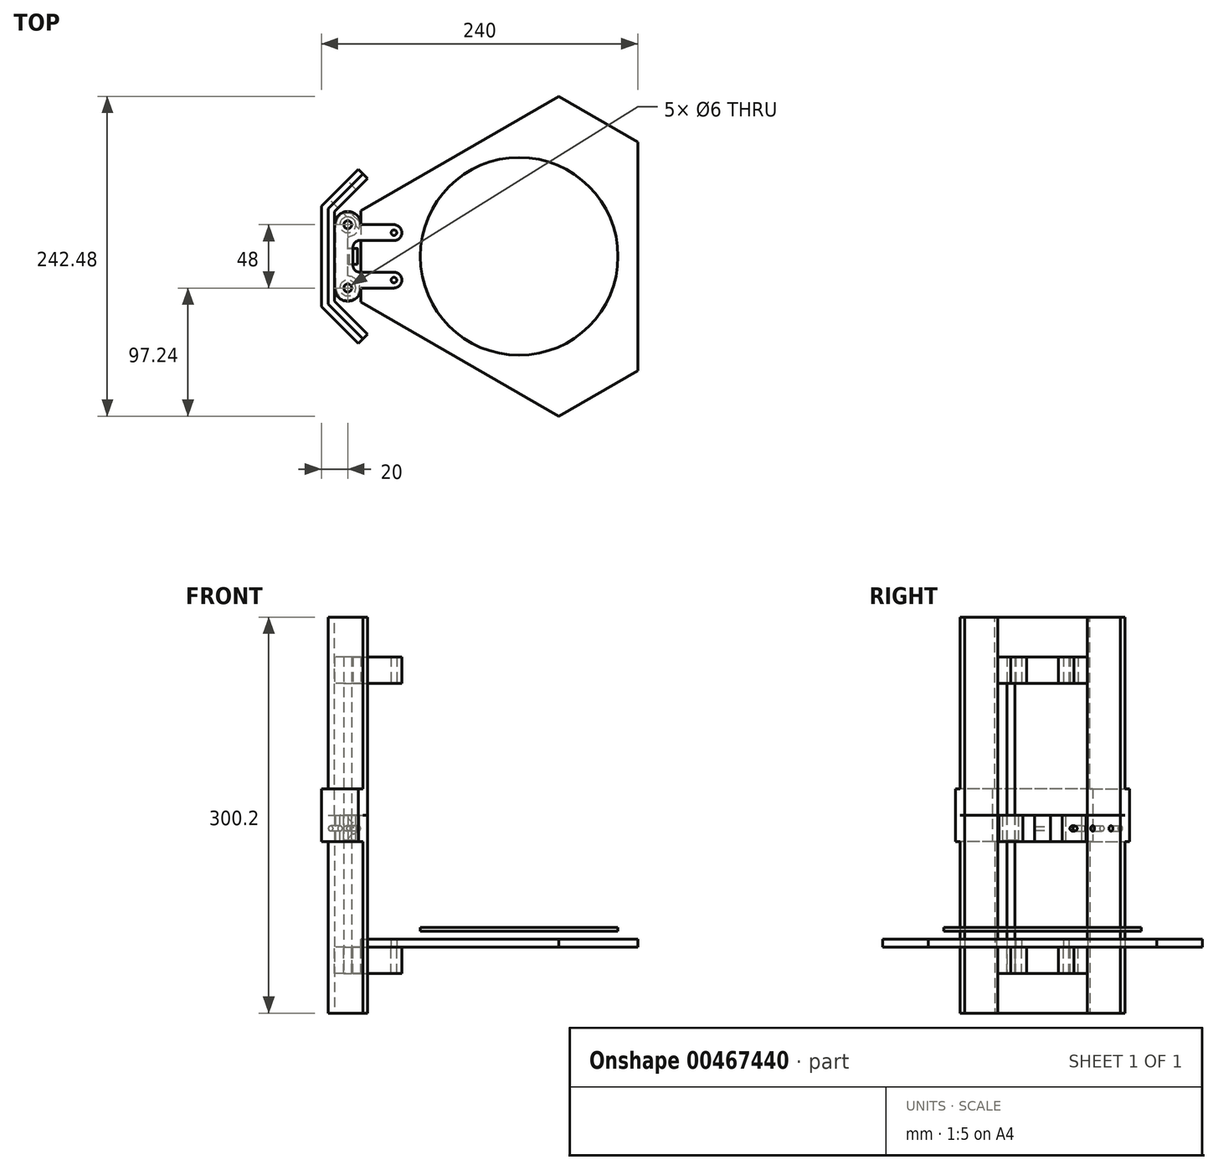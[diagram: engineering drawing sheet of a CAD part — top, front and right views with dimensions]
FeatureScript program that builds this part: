
annotation { "Feature Type Name" : "Feature", "Feature Type Description" : "" }
export const myFeature = defineFeature(function(context is Context, id is Id, definition is map)
    precondition{}
    {
        {
            var Q0;
            Q0=qCreatedBy(makeId("Top.planeOp"),FACE);
            var sketch = newSketch(context, id + "F0", { "sketchPlane" : qUnion([Q0])});
            skCircle(sketch, "E0", {"center": v(0, 0) * mm, "radius": 75 * mm});
            skSolve(sketch);
        }
        {
            var Q0;
            Q0=makeQuery(id+"F0.imprint","IMPRINT",FACE,{"disambiguationData":[TD([[makeQuery(id+"F0.imprint","IMPRINT",EDGE,{"derivedFrom":sQuery(id+"F0.wireOp",EDGE,"E0")}),1.0]])]});
            extrude(context, id + "F1", {"entities" : qUnion([Q0]), "depth" : 3 * mm});
        }
        {
            var Q0;
            Q0=qCreatedBy(makeId("Top.planeOp"),FACE);
            cPlane(context, id + "F2", {"entities" : qUnion([Q0]), "cplaneType" : CPlaneType.OFFSET, "offset" : 6 * mm, "oppositeDirection" : true, "width" : 150 * mm, "height" : 150 * mm});
        }
        {
            var Q0;
            Q0=qCreatedBy(id+"F2.planeOp",FACE);
            var sketch = newSketch(context, id + "F3", { "sketchPlane" : qUnion([Q0])});
            skLineSegment(sketch, "E1", {"start": v(30, 121.24) * mm, "end": v(-120, 34.64) * mm});
            skLineSegment(sketch, "E2", {"start": v(-120, 34.64) * mm, "end": v(-120, -34.64) * mm});
            skLineSegment(sketch, "E3", {"start": v(-120, 0) * mm, "end": v(0, 0) * mm, "construction": true});
            skLineSegment(sketch, "E4.1.0", {"start": v(30, -121.24) * mm, "end": v(90, -86.6) * mm});
            skLineSegment(sketch, "E4.1.1", {"start": v(-120, -34.64) * mm, "end": v(30, -121.24) * mm});
            skLineSegment(sketch, "E4.2.0", {"start": v(90, 86.6) * mm, "end": v(30, 121.24) * mm});
            skLineSegment(sketch, "E4.2.1", {"start": v(90, -86.6) * mm, "end": v(90, 86.6) * mm});
            skPoint(sketch, "E4.center", {"position": v(0, 0) * mm});
            skCircle(sketch, "E5", {"center": v(0, 0) * mm, "radius": 90 * mm, "construction": true});
            skSolve(sketch);
        }
        {
            var Q0;
            Q0=makeQuery(id+"F3.imprint","IMPRINT",FACE,{"disambiguationData":[TD([[makeQuery(id+"F3.imprint","IMPRINT",EDGE,{"derivedFrom":sQuery(id+"F3.wireOp",EDGE,"E1")}),1.0]])]});
            extrude(context, id + "F4", {"entities" : qUnion([Q0]), "oppositeDirection" : true, "depth" : 6 * mm});
        }
        {
            var Q0;
            Q0=makeQuery(id+"F4.opExtrude","CAP_FACE",FACE,{"disambiguationData":[OSD([sQuery(id+"F3.wireOp",EDGE,"E1"),sQuery(id+"F3.wireOp",EDGE,"E2"),sQuery(id+"F3.wireOp",EDGE,"E4.1.0"),sQuery(id+"F3.wireOp",EDGE,"E4.1.1"),sQuery(id+"F3.wireOp",EDGE,"E4.2.0"),sQuery(id+"F3.wireOp",EDGE,"E4.2.1")])],"isStart":false});
            var sketch = newSketch(context, id + "F5", { "sketchPlane" : qUnion([Q0])});
            skLineSegment(sketch, "E6", {"start": v(-120, 0) * mm, "end": v(-90, 0) * mm, "construction": true});
            skPoint(sketch, "E6.endSnap0", {"position": v(-120, 0) * mm});
            skLineSegment(sketch, "E7", {"start": v(-120, 18) * mm, "end": v(-95, 18) * mm, "construction": true});
            skArc(sketch, "E8.0.endCap", {"start": v(-95, 24) * mm, "mid": v(-89, 18) * mm, "end": v(-95, 12) * mm});
            skLineSegment(sketch, "E8.0.left", {"start": v(-120, 24) * mm, "end": v(-95, 24) * mm});
            skLineSegment(sketch, "E8.0.right", {"start": v(-119.48, 12) * mm, "end": v(-95, 12) * mm});
            skArc(sketch, "E9.MirrorCS", {"start": v(-95, -24) * mm, "mid": v(-89, -18) * mm, "end": v(-95, -12) * mm});
            skLineSegment(sketch, "E10.MirrorCS", {"start": v(-120, -24) * mm, "end": v(-95, -24) * mm});
            skLineSegment(sketch, "E11.MirrorCS", {"start": v(-119.48, -12) * mm, "end": v(-95, -12) * mm});
            skCircle(sketch, "E12", {"center": v(-95, 18) * mm, "radius": 2.1 * mm});
            skCircle(sketch, "E13", {"center": v(-95, -18) * mm, "radius": 2.1 * mm});
            skLineSegment(sketch, "E14", {"start": v(-140, 24) * mm, "end": v(-140, -24) * mm});
            skLineSegment(sketch, "E15", {"start": v(-126, 7) * mm, "end": v(-126, -7) * mm});
            skPoint(sketch, "E16.orphan", {"position": v(-120, -24) * mm});
            skPoint(sketch, "E17.MirrorCS.start.orphan", {"position": v(-119.48, -12) * mm});
            skLineSegment(sketch, "E18", {"start": v(-119.48, -12) * mm, "end": v(-121, -12) * mm});
            skLineSegment(sketch, "E19", {"start": v(-119.48, 12) * mm, "end": v(-121, 12) * mm});
            skArc(sketch, "E20", {"start": v(-121, 12) * mm, "mid": v(-124.54, 10.54) * mm, "end": v(-126, 7) * mm});
            skArc(sketch, "E21.MirrorCS", {"start": v(-121, -12) * mm, "mid": v(-124.54, -10.54) * mm, "end": v(-126, -7) * mm});
            skCircle(sketch, "E22", {"center": v(-130, -24) * mm, "radius": 3 * mm});
            skArc(sketch, "E23", {"start": v(-140, -24) * mm, "mid": v(-130, -34) * mm, "end": v(-120, -24) * mm});
            skCircle(sketch, "E24.MirrorC", {"center": v(-130, 24) * mm, "radius": 3 * mm});
            skArc(sketch, "E25.MirrorCS", {"start": v(-140, 24) * mm, "mid": v(-130, 34) * mm, "end": v(-120, 24) * mm});
            skSolve(sketch);
        }
        {
            var Q0;
            Q0=qSketchRegion(id+"F5",true);
            extrude(context, id + "F6", {"entities" : qUnion([Q0]), "depth" : 20 * mm});
        }
        {
            var Q0;
            Q0=makeQuery(id+"F4.opExtrude","CAP_FACE",FACE,{"disambiguationData":[OSD([sQuery(id+"F3.wireOp",EDGE,"E1"),sQuery(id+"F3.wireOp",EDGE,"E2"),sQuery(id+"F3.wireOp",EDGE,"E4.1.0"),sQuery(id+"F3.wireOp",EDGE,"E4.1.1"),sQuery(id+"F3.wireOp",EDGE,"E4.2.0"),sQuery(id+"F3.wireOp",EDGE,"E4.2.1")])],"isStart":false});
            cPlane(context, id + "F7", {"entities" : qUnion([Q0]), "cplaneType" : CPlaneType.OFFSET, "offset" : 50 * mm, "width" : 150 * mm, "height" : 150 * mm});
        }
        {
            var Q0;
            Q0=qCreatedBy(id+"F7.planeOp",FACE);
            var sketch = newSketch(context, id + "F8", { "sketchPlane" : qUnion([Q0])});
            skLineSegment(sketch, "E26", {"start": v(-140, -34) * mm, "end": v(-140, 34) * mm});
            skLineSegment(sketch, "E27", {"start": v(-140, 34) * mm, "end": v(-115, 59) * mm});
            skLineSegment(sketch, "E28", {"start": v(-140, 0) * mm, "end": v(-105.12, 0) * mm, "construction": true});
            skLineSegment(sketch, "E29.MirrorCS", {"start": v(-140, -34) * mm, "end": v(-115, -59) * mm});
            skLineSegment(sketch, "E30.0", {"start": v(-145, 36.07) * mm, "end": v(-118.54, 62.54) * mm});
            skLineSegment(sketch, "E30.1", {"start": v(-145, -36.07) * mm, "end": v(-145, 36.07) * mm});
            skLineSegment(sketch, "E30.2", {"start": v(-145, -36.07) * mm, "end": v(-118.54, -62.54) * mm});
            skLineSegment(sketch, "E31", {"start": v(-115, 59) * mm, "end": v(-118.54, 62.54) * mm});
            skLineSegment(sketch, "E32", {"start": v(-115, -59) * mm, "end": v(-118.54, -62.54) * mm});
            skSolve(sketch);
        }
        {
            var Q0;
            Q0=makeQuery(id+"F8.imprint","IMPRINT",FACE,{"disambiguationData":[TD([[makeQuery(id+"F8.imprint","IMPRINT",EDGE,{"derivedFrom":sQuery(id+"F8.wireOp",EDGE,"E26")}),1.0]])]});
            extrude(context, id + "F9", {"entities" : qUnion([Q0]), "operationType" : NewBodyOperationType.ADD, "oppositeDirection" : true, "depth" : 150 * mm});
        }
        {
            var Q0;
            Q0=makeQuery(id+"F9.opExtrude","CAP_FACE",FACE,{"disambiguationData":[OSD([sQuery(id+"F8.wireOp",EDGE,"E26"),sQuery(id+"F8.wireOp",EDGE,"E27"),sQuery(id+"F8.wireOp",EDGE,"E29.MirrorCS"),sQuery(id+"F8.wireOp",EDGE,"E30.0"),sQuery(id+"F8.wireOp",EDGE,"E30.1"),sQuery(id+"F8.wireOp",EDGE,"E30.2"),sQuery(id+"F8.wireOp",EDGE,"E31"),sQuery(id+"F8.wireOp",EDGE,"E32")])],"isStart":false});
            cPlane(context, id + "F10", {"entities" : qUnion([Q0]), "cplaneType" : CPlaneType.OFFSET, "offset" : .1 * mm, "width" : 150 * mm, "height" : 150 * mm});
        }
        {
            var Q0;
            Q0=makeQuery(id+"F6.opExtrude","SWEPT_BODY",BODY,{"disambiguationData":[OSD([sQuery(id+"F5.wireOp",EDGE,"E8.0.endCap"),sQuery(id+"F5.wireOp",EDGE,"E8.0.left"),sQuery(id+"F5.wireOp",EDGE,"E8.0.right"),sQuery(id+"F5.wireOp",EDGE,"E9.MirrorCS"),sQuery(id+"F5.wireOp",EDGE,"E10.MirrorCS"),sQuery(id+"F5.wireOp",EDGE,"E11.MirrorCS"),sQuery(id+"F5.wireOp",EDGE,"E12"),sQuery(id+"F5.wireOp",EDGE,"E13"),sQuery(id+"F5.wireOp",EDGE,"E14"),sQuery(id+"F5.wireOp",EDGE,"E15"),sQuery(id+"F5.wireOp",EDGE,"E18"),sQuery(id+"F5.wireOp",EDGE,"E19"),sQuery(id+"F5.wireOp",EDGE,"E20"),sQuery(id+"F5.wireOp",EDGE,"E21.MirrorCS"),sQuery(id+"F5.wireOp",EDGE,"E22"),sQuery(id+"F5.wireOp",EDGE,"E23"),sQuery(id+"F5.wireOp",EDGE,"E24.MirrorC"),sQuery(id+"F5.wireOp",EDGE,"E25.MirrorCS")])]});
            var Q1;
            Q1=qCreatedBy(id+"F10.planeOp",FACE);
            mirror(context, id + "F11", {"entities" : qUnion([Q0]), "mirrorPlane" : qUnion([Q1])});
        }
        {
            var Q0;
            Q0=qCreatedBy(id+"F10.planeOp",FACE);
            var sketch = newSketch(context, id + "F12", { "sketchPlane" : qUnion([Q0])});
            skLineSegment(sketch, "E33.0", {"start": v(-150, -38.14) * mm, "end": v(-122.07, -66.07) * mm});
            skLineSegment(sketch, "E33.1", {"start": v(-150, 38.14) * mm, "end": v(-150, -38.14) * mm});
            skLineSegment(sketch, "E33.2", {"start": v(-150, 38.14) * mm, "end": v(-122.07, 66.07) * mm});
            skLineSegment(sketch, "E34.0", {"start": v(-145, -36.07) * mm, "end": v(-118.54, -62.54) * mm});
            skLineSegment(sketch, "E35.0", {"start": v(-145, 36.07) * mm, "end": v(-145, -36.07) * mm});
            skLineSegment(sketch, "E36.0", {"start": v(-145, 36.07) * mm, "end": v(-118.54, 62.54) * mm});
            skLineSegment(sketch, "E37", {"start": v(-122.07, -66.07) * mm, "end": v(-118.54, -62.54) * mm});
            skLineSegment(sketch, "E38", {"start": v(-122.07, 66.07) * mm, "end": v(-118.54, 62.54) * mm});
            skSolve(sketch);
        }
        {
            var Q0;
            Q0=qSketchRegion(id+"F12",true);
            extrude(context, id + "F13", {"entities" : qUnion([Q0]), "operationType" : NewBodyOperationType.ADD, "endBound" : BoundingType.SYMMETRIC, "depth" : 40 * mm});
        }
        {
            var Q0;
            Q0=makeQuery(id+"F6.opExtrude","CAP_FACE",FACE,{"disambiguationData":[OSD([sQuery(id+"F5.wireOp",EDGE,"E8.0.endCap"),sQuery(id+"F5.wireOp",EDGE,"E8.0.left"),sQuery(id+"F5.wireOp",EDGE,"E8.0.right"),sQuery(id+"F5.wireOp",EDGE,"E9.MirrorCS"),sQuery(id+"F5.wireOp",EDGE,"E10.MirrorCS"),sQuery(id+"F5.wireOp",EDGE,"E11.MirrorCS"),sQuery(id+"F5.wireOp",EDGE,"E12"),sQuery(id+"F5.wireOp",EDGE,"E13"),sQuery(id+"F5.wireOp",EDGE,"E14"),sQuery(id+"F5.wireOp",EDGE,"E15"),sQuery(id+"F5.wireOp",EDGE,"E18"),sQuery(id+"F5.wireOp",EDGE,"E19"),sQuery(id+"F5.wireOp",EDGE,"E20"),sQuery(id+"F5.wireOp",EDGE,"E21.MirrorCS"),sQuery(id+"F5.wireOp",EDGE,"E22"),sQuery(id+"F5.wireOp",EDGE,"E23"),sQuery(id+"F5.wireOp",EDGE,"E24.MirrorC"),sQuery(id+"F5.wireOp",EDGE,"E25.MirrorCS")])],"isStart":false});
            var sketch = newSketch(context, id + "F14", { "sketchPlane" : qUnion([Q0])});
            skCircle(sketch, "E39.0", {"center": v(-130, 24) * mm, "radius": 3 * mm});
            skSolve(sketch);
        }
        {
            var Q0;
            Q0=qSketchRegion(id+"F14",true);
            var Q1;
            Q1=makeQuery(id+"F11.opPattern","COPY",FACE,{"derivedFrom":makeQuery(id+"F6.opExtrude","CAP_FACE",FACE,{"disambiguationData":[OSD([sQuery(id+"F5.wireOp",EDGE,"E8.0.endCap"),sQuery(id+"F5.wireOp",EDGE,"E8.0.left"),sQuery(id+"F5.wireOp",EDGE,"E8.0.right"),sQuery(id+"F5.wireOp",EDGE,"E9.MirrorCS"),sQuery(id+"F5.wireOp",EDGE,"E10.MirrorCS"),sQuery(id+"F5.wireOp",EDGE,"E11.MirrorCS"),sQuery(id+"F5.wireOp",EDGE,"E12"),sQuery(id+"F5.wireOp",EDGE,"E13"),sQuery(id+"F5.wireOp",EDGE,"E14"),sQuery(id+"F5.wireOp",EDGE,"E15"),sQuery(id+"F5.wireOp",EDGE,"E18"),sQuery(id+"F5.wireOp",EDGE,"E19"),sQuery(id+"F5.wireOp",EDGE,"E20"),sQuery(id+"F5.wireOp",EDGE,"E21.MirrorCS"),sQuery(id+"F5.wireOp",EDGE,"E22"),sQuery(id+"F5.wireOp",EDGE,"E23"),sQuery(id+"F5.wireOp",EDGE,"E24.MirrorC"),sQuery(id+"F5.wireOp",EDGE,"E25.MirrorCS")])],"isStart":false}),"instanceName":"1"});
            extrude(context, id + "F15", {"entities" : qUnion([Q0]), "endBound" : BoundingType.UP_TO_SURFACE, "oppositeDirection" : true, "endBoundEntityFace" : qUnion([Q1]), "depth" : 25 * mm});
        }
        {
            var Q0;
            Q0=qCreatedBy(id+"F10.planeOp",FACE);
            var sketch = newSketch(context, id + "F16", { "sketchPlane" : qUnion([Q0])});
            skCircle(sketch, "E40", {"center": v(-130, -24) * mm, "radius": 6.05 * mm});
            skCircle(sketch, "E41", {"center": v(-130, -24) * mm, "radius": 3 * mm, "construction": true});
            skArc(sketch, "E42", {"start": v(-139, -24) * mm, "mid": v(-123.64, -30.36) * mm, "end": v(-130, -15) * mm});
            skLineSegment(sketch, "E43", {"start": v(-111.99, 0) * mm, "end": v(-93.99, 0) * mm});
            skArc(sketch, "E44.MirrorC", {"start": v(-139, 24) * mm, "mid": v(-123.64, 30.36) * mm, "end": v(-130, 15) * mm});
            skCircle(sketch, "E45.MirrorC", {"center": v(-130, 24) * mm, "radius": 6.05 * mm});
            skLineSegment(sketch, "E46", {"start": v(-139, -24) * mm, "end": v(-139, 24) * mm});
            skLineSegment(sketch, "E47.trimOffspring", {"start": v(-130, -15) * mm, "end": v(-130, 15) * mm});
            skSolve(sketch);
        }
        {
            var Q0;
            Q0=makeQuery(id+"F16.imprint","IMPRINT",FACE,{"disambiguationData":[TD([[makeQuery(id+"F16.imprint","IMPRINT",EDGE,{"derivedFrom":sQuery(id+"F16.wireOp",EDGE,"E40")}),-1.0]])]});
            extrude(context, id + "F17", {"entities" : qUnion([Q0]), "oppositeDirection" : true, "depth" : 20 * mm});
        }
        {
            var Q0;
            Q0=makeQuery(id+"F17.opExtrude","CAP_FACE",FACE,{"disambiguationData":[OSD([sQuery(id+"F16.wireOp",EDGE,"E40"),sQuery(id+"F16.wireOp",EDGE,"E42"),sQuery(id+"F16.wireOp",EDGE,"E44.MirrorC"),sQuery(id+"F16.wireOp",EDGE,"E45.MirrorC"),sQuery(id+"F16.wireOp",EDGE,"E46"),sQuery(id+"F16.wireOp",EDGE,"E47.trimOffspring")])],"isStart":true});
            var sketch = newSketch(context, id + "F18", { "sketchPlane" : qUnion([Q0])});
            skCircle(sketch, "E48", {"center": v(-130, -24) * mm, "radius": 3 * mm});
            skCircle(sketch, "E49", {"center": v(-130, -24) * mm, "radius": 6 * mm});
            skSolve(sketch);
        }
        {
            var Q0;
            Q0=makeQuery(id+"F18.imprint","IMPRINT",FACE,{"disambiguationData":[TD([[makeQuery(id+"F18.imprint","IMPRINT",EDGE,{"derivedFrom":sQuery(id+"F18.wireOp",EDGE,"E48")}),-1.0]])]});
            extrude(context, id + "F19", {"entities" : qUnion([Q0]), "oppositeDirection" : true, "depth" : 19 * mm});
        }
        {
            var Q0;
            Q0=makeQuery(id+"F13.opExtrude","SWEPT_FACE",FACE,{"disambiguationData":[OSD([sQuery(id+"F12.wireOp",EDGE,"E33.2")])]});
            var sketch = newSketch(context, id + "F20", { "sketchPlane" : qUnion([Q0])});
            skCircle(sketch, "E50", {"center": v(69.15, 78.05) * mm, "radius": 2.1 * mm});
            skLineSegment(sketch, "E51", {"start": v(69.15, 78.05) * mm, "end": v(49.55, 78.05) * mm, "construction": true});
            skCircle(sketch, "E52", {"center": v(49.55, 78.05) * mm, "radius": 2.1 * mm});
            skCircle(sketch, "E53", {"center": v(49.55, 78.05) * mm, "radius": 9.95 * mm, "construction": true});
            skCircle(sketch, "E54", {"center": v(69.15, 78.05) * mm, "radius": 9.95 * mm, "construction": true});
            skSolve(sketch);
        }
        {
            var Q0;
            Q0=qSketchRegion(id+"F20",true);
            extrude(context, id + "F21", {"entities" : qUnion([Q0]), "operationType" : NewBodyOperationType.REMOVE, "endBound" : BoundingType.THROUGH_ALL, "oppositeDirection" : true, "depth" : 25 * mm});
        }
        {
            var Q0;
            Q0=qCreatedBy(makeId("Front.planeOp"),FACE);
            var sketch = newSketch(context, id + "F22", { "sketchPlane" : qUnion([Q0])});
            skCircle(sketch, "E55", {"center": v(-127, 78.1) * mm, "radius": 1.5 * mm});
            skCircle(sketch, "E56", {"center": v(-127, 78.1) * mm, "radius": 4.5 * mm});
            skLineSegment(sketch, "E57", {"start": v(-127, 78.1) * mm, "end": v(-130, 78.1) * mm, "construction": true});
            skSolve(sketch);
        }
        {
            var Q0;
            Q0=qSketchRegion(id+"F22",true);
            extrude(context, id + "F23", {"entities" : qUnion([Q0]), "operationType" : NewBodyOperationType.ADD, "endBound" : BoundingType.SYMMETRIC, "depth" : 12 * mm});
        }
        {
            var Q0;
            Q0=makeQuery(id+"F23.boolean.opBoolean","INTERSECT",EDGE,{"disambiguationData":[OD(1.0)],"derivedFrom":[makeQuery(id+"F17.opExtrude","SWEPT_FACE",FACE,{"disambiguationData":[OSD([sQuery(id+"F16.wireOp",EDGE,"E47.trimOffspring")])]}),makeQuery(id+"F23.opExtrude","SWEPT_FACE",FACE,{"disambiguationData":[OSD([sQuery(id+"F22.wireOp",EDGE,"E56")])]})]});
            var Q1;
            Q1=makeQuery(id+"F23.boolean.opBoolean","INTERSECT",EDGE,{"disambiguationData":[OD(0.0)],"derivedFrom":[makeQuery(id+"F17.opExtrude","SWEPT_FACE",FACE,{"disambiguationData":[OSD([sQuery(id+"F16.wireOp",EDGE,"E47.trimOffspring")])]}),makeQuery(id+"F23.opExtrude","SWEPT_FACE",FACE,{"disambiguationData":[OSD([sQuery(id+"F22.wireOp",EDGE,"E56")])]})]});
            fillet(context, id + "F24", {"entities" : qUnion([Q0, Q1]), "radius" : 6 * mm, "tangentPropagation" : true, "allowEdgeOverflow" : false});
        }
        {
            var Q0;
            Q0=makeQuery(id+"F4.opExtrude","CAP_FACE",FACE,{"disambiguationData":[OSD([sQuery(id+"F3.wireOp",EDGE,"E1"),sQuery(id+"F3.wireOp",EDGE,"E2"),sQuery(id+"F3.wireOp",EDGE,"E4.1.0"),sQuery(id+"F3.wireOp",EDGE,"E4.1.1"),sQuery(id+"F3.wireOp",EDGE,"E4.2.0"),sQuery(id+"F3.wireOp",EDGE,"E4.2.1")])],"isStart":false});
            var sketch = newSketch(context, id + "F25", { "sketchPlane" : qUnion([Q0])});
            skCircle(sketch, "E58.0", {"center": v(-95, 18) * mm, "radius": 2.1 * mm});
            skCircle(sketch, "E59.0", {"center": v(-95, -18) * mm, "radius": 2.1 * mm});
            skSolve(sketch);
        }
        {
            var Q0;
            Q0=qSketchRegion(id+"F25",true);
            extrude(context, id + "F26", {"entities" : qUnion([Q0]), "operationType" : NewBodyOperationType.REMOVE, "oppositeDirection" : true, "depth" : 25 * mm});
        }
        {
            var Q0;
            Q0=qCreatedBy(makeId("Right.planeOp"),FACE);
            var sketch = newSketch(context, id + "F27", { "sketchPlane" : qUnion([Q0])});
            skLineSegment(sketch, "E60", {"start": v(0, 0) * mm, "end": v(0, 66.25) * mm});
            skSolve(sketch);
        }
    });
